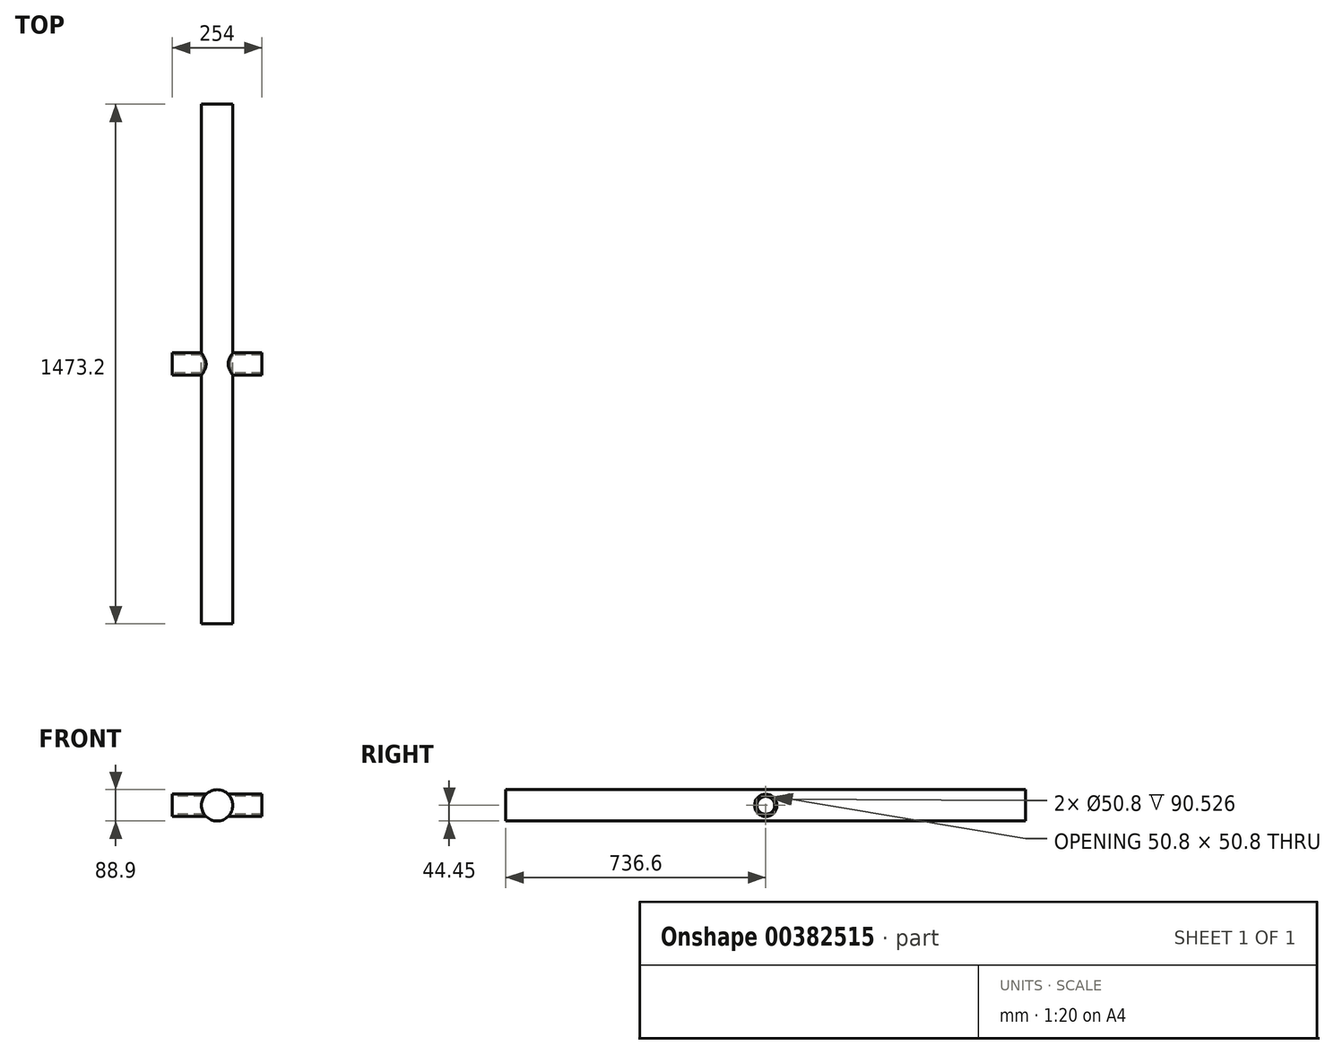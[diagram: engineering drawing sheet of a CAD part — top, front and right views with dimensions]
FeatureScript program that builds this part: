
annotation { "Feature Type Name" : "Feature", "Feature Type Description" : "" }
export const myFeature = defineFeature(function(context is Context, id is Id, definition is map)
    precondition{}
    {
        {
            var Q0;
            Q0=qCreatedBy(makeId("Front.planeOp"),FACE);
            var sketch = newSketch(context, id + "F0", { "sketchPlane" : qUnion([Q0])});
            skCircle(sketch, "E0", {"center": v(0, 0) * mm, "radius": 44.45 * mm});
            skSolve(sketch);
        }
        {
            var Q0;
            Q0=qSketchRegion(id+"F0",true);
            extrude(context, id + "F1", {"entities" : qUnion([Q0]), "depth" : 25.4 * mm});
        }
        {
            var Q0;
            Q0=qSketchRegion(id+"F0",true);
            extrude(context, id + "F2", {"entities" : qUnion([Q0]), "operationType" : NewBodyOperationType.ADD, "depth" : 1473.2 * mm});
        }
        {
            var Q0;
            Q0=qCreatedBy(makeId("Right.planeOp"),FACE);
            var sketch = newSketch(context, id + "F3", { "sketchPlane" : qUnion([Q0])});
            skCircle(sketch, "E1", {"center": v(-736.6, 0) * mm, "radius": 25.4 * mm});
            skCircle(sketch, "E2.0", {"center": v(-736.6, 0) * mm, "radius": 31.75 * mm});
            skSolve(sketch);
        }
        {
            var Q0;
            Q0=qSketchRegion(id+"F3",true);
            extrude(context, id + "F4", {"entities" : qUnion([Q0]), "operationType" : NewBodyOperationType.ADD, "depth" : 127 * mm, "hasSecondDirection" : true, "secondDirectionOppositeDirection" : true, "secondDirectionDepth" : 127 * mm});
        }
    });
